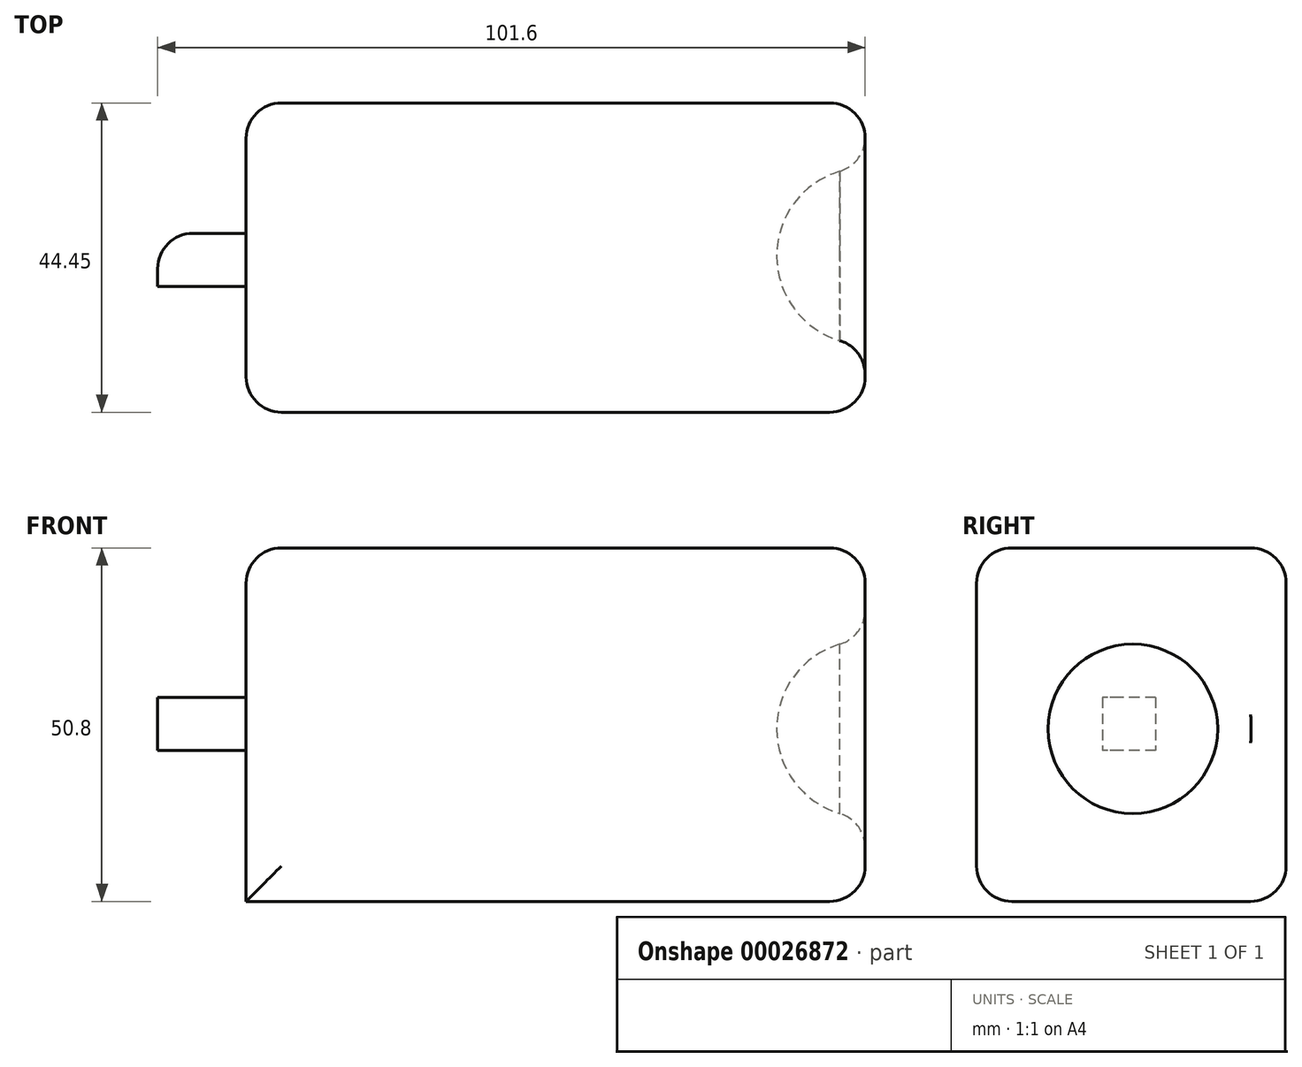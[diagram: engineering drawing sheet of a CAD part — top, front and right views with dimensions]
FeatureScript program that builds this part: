
annotation { "Feature Type Name" : "Feature", "Feature Type Description" : "" }
export const myFeature = defineFeature(function(context is Context, id is Id, definition is map)
    precondition{}
    {
        {
            var Q0;
            Q0=qCreatedBy(makeId("Front.planeOp"),FACE);
            var sketch = newSketch(context, id + "F0", { "sketchPlane" : qUnion([Q0])});
            skLineSegment(sketch, "E0.bottom", {"start": v(-43.4, 40.76) * mm, "end": v(45.5, 40.76) * mm});
            skLineSegment(sketch, "E0.top", {"start": v(-43.4, -10.04) * mm, "end": v(45.5, -10.04) * mm});
            skLineSegment(sketch, "E0.left", {"start": v(-43.4, 40.76) * mm, "end": v(-43.4, -10.04) * mm});
            skLineSegment(sketch, "E0.right", {"start": v(45.5, 40.76) * mm, "end": v(45.5, -10.04) * mm});
            skSolve(sketch);
        }
        {
            var Q0;
            Q0 = qSketchRegion(id + "F0", true);
            extrude(context, id + "F1", {"entities" : qUnion([Q0]), "depth" : 44.45 * mm});
        }
        {
            var Q0;
            Q0=makeQuery(id+"F1.opExtrude","SWEPT_FACE",FACE,{"disambiguationData":[OSD([sQuery(id+"F0.wireOp",EDGE,"E0.right")])]});
            var sketch = newSketch(context, id + "F2", { "sketchPlane" : qUnion([Q0])});
            skCircle(sketch, "E1", {"center": v(-22, 14.76) * mm, "radius": 12.7 * mm});
            skLineSegment(sketch, "E2", {"start": v(-22, 27.46) * mm, "end": v(-22, 2.06) * mm});
            skSolve(sketch);
        }
        {
            var Q0;
            {var subQ0=sQuery(id+"F2.wireOp",EDGE,"E2");Q0=makeQuery(id+"F2.imprint","IMPRINT",FACE,{"disambiguationData":[TD([[makeQuery(id+"F2.imprint","IMPRINT",EDGE,{"derivedFrom":subQ0}),-1.0]])]});}
            var Q1;
            Q1=sQuery(id+"F2.wireOp",EDGE,"E2");
            revolve(context, id + "F3", {"operationType" : NewBodyOperationType.REMOVE, "entities" : qUnion([Q0]), "axis" : qUnion([Q1]), "revolveType" : RevolveType.FULL, "oppositeDirection" : true});
        }
        {
            var Q0;
            Q0=makeQuery(id+"F1.opExtrude","SWEPT_FACE",FACE,{"disambiguationData":[OSD([sQuery(id+"F0.wireOp",EDGE,"E0.left")])]});
            var sketch = newSketch(context, id + "F4", { "sketchPlane" : qUnion([Q0])});
            skLineSegment(sketch, "E3.bottom", {"start": v(18.74, 19.24) * mm, "end": v(26.36, 19.24) * mm});
            skLineSegment(sketch, "E3.top", {"start": v(18.74, 11.62) * mm, "end": v(26.36, 11.62) * mm});
            skLineSegment(sketch, "E3.left", {"start": v(18.74, 19.24) * mm, "end": v(18.74, 11.62) * mm});
            skLineSegment(sketch, "E3.right", {"start": v(26.36, 19.24) * mm, "end": v(26.36, 11.62) * mm});
            skSolve(sketch);
        }
        {
            var Q0;
            Q0 = qSketchRegion(id + "F4", true);
            extrude(context, id + "F5", {"entities" : qUnion([Q0]), "operationType" : NewBodyOperationType.ADD, "depth" : 12.7 * mm});
        }
        {
            var Q0;
            Q0=makeQuery(id+"F1.opExtrude","SWEPT_FACE",FACE,{"disambiguationData":[OSD([sQuery(id+"F0.wireOp",EDGE,"E0.bottom")])]});
            var Q1;
            Q1=makeQuery(id+"F1.opExtrude","SWEPT_EDGE",EDGE,{"disambiguationData":[OSD([sQuery(id+"F0.wireOp",EDGE,"E0.top"),sQuery(id+"F0.wireOp",EDGE,"E0.right")])]});
            var Q2;
            Q2=makeQuery(id+"F1.opExtrude","CAP_EDGE",EDGE,{"disambiguationData":[OSD([sQuery(id+"F0.wireOp",EDGE,"E0.top")])],"isStart":false});
            var Q3;
            Q3=makeQuery(id+"F1.opExtrude","CAP_EDGE",EDGE,{"disambiguationData":[OSD([sQuery(id+"F0.wireOp",EDGE,"E0.left")])],"isStart":false});
            var Q4;
            Q4=makeQuery(id+"F1.opExtrude","CAP_EDGE",EDGE,{"disambiguationData":[OSD([sQuery(id+"F0.wireOp",EDGE,"E0.top")])],"isStart":true});
            var Q5;
            Q5=makeQuery(id+"F1.opExtrude","CAP_EDGE",EDGE,{"disambiguationData":[OSD([sQuery(id+"F0.wireOp",EDGE,"E0.left")])],"isStart":true});
            var Q6;
            Q6=makeQuery(id+"F5.opExtrude","CAP_EDGE",EDGE,{"disambiguationData":[OSD([sQuery(id+"F4.wireOp",EDGE,"E3.left")])],"isStart":false});
            var Q7;
            Q7=makeQuery(id+"F3.boolean.opBoolean","COPY",FACE,{"derivedFrom":makeQuery(id+"F3.opRevolve","SWEPT_FACE",FACE,{"disambiguationData":[OSD([sQuery(id+"F2.wireOp",EDGE,"E1")])]})});
            var Q8;
            Q8=makeQuery(id+"F1.opExtrude","CAP_EDGE",EDGE,{"disambiguationData":[OSD([sQuery(id+"F0.wireOp",EDGE,"E0.right")])],"isStart":true});
            var Q9;
            Q9=makeQuery(id+"F1.opExtrude","CAP_EDGE",EDGE,{"disambiguationData":[OSD([sQuery(id+"F0.wireOp",EDGE,"E0.right")])],"isStart":false});
            fillet(context, id + "F6", {"entities" : qUnion([Q0, Q1, Q2, Q3, Q4, Q5, Q6, Q7, Q8, Q9]), "radius" : 5.08 * mm, "tangentPropagation" : true, "allowEdgeOverflow" : false});
        }
    });
